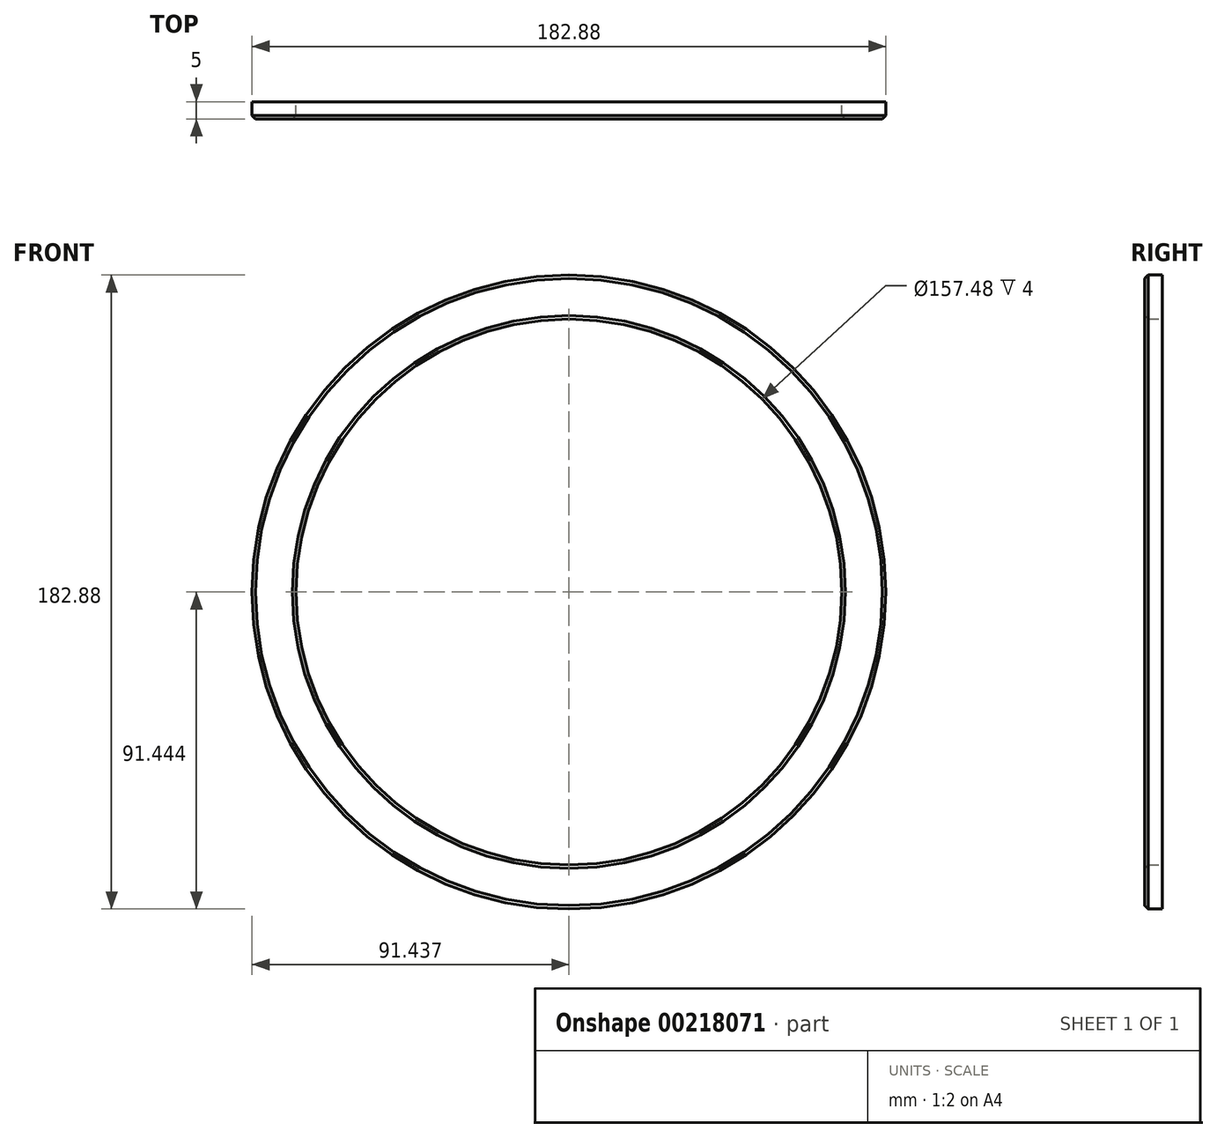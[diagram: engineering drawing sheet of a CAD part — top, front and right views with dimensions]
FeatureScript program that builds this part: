
annotation { "Feature Type Name" : "Feature", "Feature Type Description" : "" }
export const myFeature = defineFeature(function(context is Context, id is Id, definition is map)
    precondition{}
    {
        {
            var Q0;
            Q0=qCreatedBy(makeId("Front.planeOp"),FACE);
            var sketch = newSketch(context, id + "F0", { "sketchPlane" : qUnion([Q0])});
            skCircle(sketch, "E0", {"center": v(-18.1, 4.9) * mm, "radius": 78.74 * mm});
            skCircle(sketch, "E1", {"center": v(-18.1, 4.9) * mm, "radius": 91.44 * mm});
            skSolve(sketch);
        }
        {
            var Q0;
            Q0=makeQuery(id+"F0.imprint","IMPRINT",FACE,{"disambiguationData":[TD([[makeQuery(id+"F0.imprint","IMPRINT",EDGE,{"derivedFrom":sQuery(id+"F0.wireOp",EDGE,"E0")}),-1.0]])]});
            extrude(context, id + "F1", {"entities" : qUnion([Q0]), "depth" : 5 * mm});
        }
        {
            var Q0;
            Q0=makeQuery(id+"F1.opExtrude","CAP_EDGE",EDGE,{"disambiguationData":[OSD([sQuery(id+"F0.wireOp",EDGE,"E1")])],"isStart":false});
            chamfer(context, id + "F2", {"entities" : qUnion([Q0]), "width" : 1 * mm, "tangentPropagation" : true});
        }
        {
            var Q0;
            Q0=makeQuery(id+"F1.opExtrude","CAP_EDGE",EDGE,{"disambiguationData":[OSD([sQuery(id+"F0.wireOp",EDGE,"E0")])],"isStart":false});
            chamfer(context, id + "F3", {"entities" : qUnion([Q0]), "width" : 1 * mm, "tangentPropagation" : true});
        }
    });
